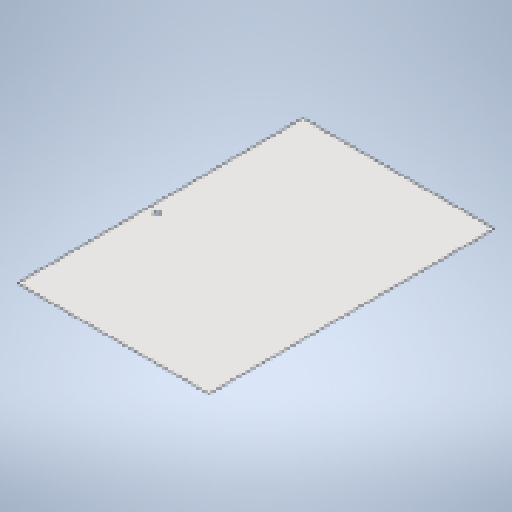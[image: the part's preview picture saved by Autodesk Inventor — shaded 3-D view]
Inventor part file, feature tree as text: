
AUTODESK INVENTOR PART (.ipt)
format: ipt  version: 2025 (Build 290162010, 162A)  size: 173,056 bytes
history: native  units: mm
features: sketch x2, other x2, sheet_metal_op x1, extrude x1
ambient origin geometry x8: Origin, YZ Plane, XZ Plane, XY Plane, X Axis, Y Axis, Z Axis, Center Point
bodies: Solid1 (feature_tree)
feature tree (6):
  sheet_metal_op  "Face1"
  extrude  "Extrusion2"  Depth=2980.0mm
  sketch  "Sketch1"  dims[d0=2000.0mm d1=2980.0mm]
  other  "Plate1"
  sketch  "Sketch6"  dims[d2=3.0mm d36=65.0mm d37=1620.0mm d39=10.0mm d40=0.0mm d41=100.0mm]
  other  "Definition1"
